# Revit family: 5.Электрический нагреватель для прямоугольных каналов ELN
name_source: partatom
category: Оборудование
revit_build: Autodesk Revit 2016 (Build: 20151209_0715(x64)
units: mm (PartAtom-declared; Revit-internal decimal feet)

## family parameters
Всегда вертикально = Да
На основе рабочей плоскости = Нет
Общий = Нет
При загрузке вырезать с полостями = Нет
Размер круглого соединителя = Использовать диаметр
Тип детали = Нормальный
Точка расчета площади = Нет

## types (29) — shared parameters
d = 15 мм
Единица измерения = шт.
Завод изготовитель = KORF
Ключевая пометка = Вентиляция
Материал = Сталь серая
Наименование и тех.хар-ка = Электрический нагреватель для прямоугольных каналов
Раздел = ОВ

## per-type parameters (varying)
| type | А | Б | Б2 | Высота | Г | Глубина среза | Д | Е | Ж | Ж2 | И | И1 | К | Масса единицы | Мощность, кВт | Напряжение U,В | Размер В | Сила тока J, А | Тип, марка, обозначение | Ширина |
| 30-15/3 | 300 мм | 150 мм | 21 мм | 150 мм | 170 мм | 15 мм | 340 мм | 190 мм | 410 мм | 35 мм | 360 мм | 356 мм | 9 мм | 7 кг | 3 Вт | 1-220 | 320 мм | 13,1 | ELN 30-15/3 | 300 мм |
| 30-15/4.5 | 300 мм | 150 мм | 21 мм | 150 мм | 170 мм | 15 мм | 340 мм | 190 мм | 410 мм | 35 мм | 360 мм | 356 мм | 9 мм | 7.4 кг | 5 Вт | 1-220 | 320 мм | 19,1 | ELN 30-15/4.5 | 300 мм |
| 40-20/6 | 400 мм | 200 мм | 27 мм | 200 мм | 220 мм | 15 мм | 440 мм | 240 мм | 510 мм | 35 мм | 390 мм | 386 мм | 9 мм | 16 кг | 6 Вт | 3-380 | 420 мм | 9,1 | ELN 40-20/6 | 400 мм |
| 40-20/12 | 400 мм | 200 мм | 27 мм | 200 мм | 220 мм | 15 мм | 440 мм | 240 мм | 510 мм | 35 мм | 510 мм | 506 мм | 9 мм | 16 кг | 12 Вт | 3-380 | 420 мм | 18,1 | ELN 40-20/12 | 400 мм |
| 50-25/7.5 | 500 мм | 250 мм | 32 мм | 250 мм | 270 мм | 15 мм | 540 мм | 290 мм | 610 мм | 35 мм | 390 мм | 386 мм | 9 мм | 11 кг | 8 Вт | 3-380 | 520 мм | 11,3 | ELN 50-25/7.5 | 500 мм |
| 50-25/15 | 500 мм | 250 мм | 32 мм | 250 мм | 270 мм | 15 мм | 540 мм | 290 мм | 610 мм | 35 мм | 510 мм | 506 мм | 9 мм | 15 кг | 15 Вт | 3-380 | 520 мм | 22,6 | ELN 50-25/15 | 500 мм |
| 50-25/22.5 | 500 мм | 250 мм | 32 мм | 250 мм | 270 мм | 15 мм | 540 мм | 290 мм | 610 мм | 35 мм | 630 мм | 626 мм | 9 мм | 19 кг | 23 Вт | 3-380 | 520 мм | 33,9 | ELN 50-25/22.5 | 500 мм |
| 50-30/7.5 | 500 мм | 300 мм | 38 мм | 300 мм | 320 мм | 15 мм | 540 мм | 340 мм | 610 мм | 35 мм | 390 мм | 386 мм | 9 мм | 11.5 кг | 8 Вт | 3-380 | 520 мм | 11,3 | ELN 50-30/7.5 | 500 мм |
| 50-30/15 | 500 мм | 300 мм | 38 мм | 300 мм | 320 мм | 15 мм | 540 мм | 340 мм | 610 мм | 35 мм | 510 мм | 506 мм | 9 мм | 15.7 кг | 15 Вт | 3-380 | 520 мм | 22,6 | ELN 50-30/15 | 500 мм |
| 50-30/22.5 | 500 мм | 300 мм | 38 мм | 300 мм | 320 мм | 15 мм | 540 мм | 340 мм | 610 мм | 35 мм | 630 мм | 626 мм | 9 мм | 19.8 кг | 23 Вт | 3-380 | 520 мм | 33,9 | ELN 50-30/22.5 | 500 мм |
| 60-30/15 | 600 мм | 300 мм | 38 мм | 300 мм | 320 мм | 15 мм | 640 мм | 340 мм | 710 мм | 35 мм | 510 мм | 506 мм | 9 мм | 16.8 кг | 15 Вт | 3-380 | 620 мм | 22,6 | ELN 60-30/15 | 600 мм |
| 60-30/22.5 | 600 мм | 300 мм | 38 мм | 300 мм | 320 мм | 15 мм | 640 мм | 340 мм | 710 мм | 35 мм | 630 мм | 626 мм | 9 мм | 22.4 кг | 23 Вт | 3-380 | 620 мм | 33,9 | ELN 60-30/22.5 | 600 мм |
| 60-30/30 | 600 мм | 300 мм | 38 мм | 300 мм | 320 мм | 15 мм | 640 мм | 340 мм | 710 мм | 35 мм | 750 мм | 746 мм | 9 мм | 26.4 кг | 30 Вт | 3-380 | 620 мм | 45,1 | ELN 60-30/30 | 600 мм |
| 60-35/15 | 600 мм | 350 мм | 43 мм | 350 мм | 370 мм | 15 мм | 640 мм | 390 мм | 710 мм | 35 мм | 510 мм | 506 мм | 9 мм | 17.5 кг | 15 Вт | 3-380 | 620 мм | 22,6 | ELN 60-35/15 | 600 мм |
| 60-35/22.5 | 600 мм | 350 мм | 43 мм | 350 мм | 370 мм | 15 мм | 640 мм | 390 мм | 710 мм | 35 мм | 630 мм | 626 мм | 9 мм | 24.6 кг | 23 Вт | 3-380 | 620 мм | 33,9 | ELN 60-35/22.5 | 600 мм |
| 60-35/30 | 600 мм | 350 мм | 43 мм | 350 мм | 370 мм | 15 мм | 640 мм | 390 мм | 710 мм | 35 мм | 750 мм | 746 мм | 9 мм | 28.4 кг | 30 Вт | 3-380 | 620 мм | 45,1 | ELN 60-35/30 | 600 мм |
| 70-40/15 | 700 мм | 400 мм | 49 мм | 400 мм | 420 мм | 15 мм | 740 мм | 440 мм | 812 мм | 36 мм | 510 мм | 506 мм | 9 мм | 26.7 кг | 15 Вт | 3-380 | 720 мм | 22,6 | ELN 70-40/15 | 700 мм |
| 70-40/30 | 700 мм | 400 мм | 49 мм | 400 мм | 420 мм | 15 мм | 740 мм | 440 мм | 812 мм | 36 мм | 510 мм | 506 мм | 9 мм | 27.1 кг | 30 Вт | 3-380 | 720 мм | 45,1 | ELN 70-40/30 | 700 мм |
| 70-40/45 | 700 мм | 400 мм | 49 мм | 400 мм | 420 мм | 15 мм | 740 мм | 440 мм | 830 мм | 45 мм | 750 мм | 746 мм | 9 мм | 41.2 кг | 45 Вт | 3-380 | 720 мм | 67,6 | ELN 70-40/45 | 700 мм |
| 70-40/60 | 700 мм | 400 мм | 49 мм | 400 мм | 420 мм | 15 мм | 740 мм | 440 мм | 830 мм | 45 мм | 750 мм | 746 мм | 9 мм | 41.2 кг | 60 Вт | 3-380 | 720 мм | 90,1 | ELN 70-40/60 | 700 мм |
| 80-50/15 | 800 мм | 500 мм | 60 мм | 500 мм | 520 мм | 15 мм | 840 мм | 540 мм | 910 мм | 35 мм | 510 мм | 506 мм | 9 мм | 31.1 кг | 15 Вт | 3-380 | 820 мм | 22,6 | ELN 80-50/15 | 800 мм |
| 80-50/30 | 800 мм | 500 мм | 60 мм | 500 мм | 520 мм | 15 мм | 840 мм | 540 мм | 910 мм | 35 мм | 510 мм | 506 мм | 9 мм | 31.4 кг | 30 Вт | 3-380 | 820 мм | 45,1 | ELN 80-50/30 | 800 мм |
| 80-50/45 | 800 мм | 500 мм | 60 мм | 500 мм | 520 мм | 15 мм | 840 мм | 540 мм | 930 мм | 45 мм | 750 мм | 746 мм | 9 мм | 45.2 кг | 45 Вт | 3-380 | 820 мм | 67,6 | ELN 80-50/45 | 800 мм |
| 80-50/60 | 800 мм | 500 мм | 60 мм | 500 мм | 520 мм | 15 мм | 840 мм | 540 мм | 930 мм | 45 мм | 750 мм | 746 мм | 9 мм | 45.2 кг | 60 Вт | 3-380 | 820 мм | 90,1 | ELN 80-50/60 | 800 мм |
| 90-50/30 | 900 мм | 500 мм | 62 мм | 500 мм | 530 мм | 16 мм | 960 мм | 560 мм | 960 мм | 0 мм | 513 мм | 509 мм | 11 мм | 31.5 кг | 30 Вт | 3-380 | 930 мм | 45,1 | ELN 90-50/30 | 900 мм |
| 90-50/45 | 900 мм | 500 мм | 62 мм | 500 мм | 530 мм | 16 мм | 960 мм | 560 мм | 960 мм | 0 мм | 753 мм | 749 мм | 11 мм | 49.8 кг | 45 Вт | 3-380 | 930 мм | 67,6 | ELN 90-50/45 | 900 мм |
| 90-50/60 | 900 мм | 500 мм | 62 мм | 500 мм | 530 мм | 16 мм | 960 мм | 560 мм | 960 мм | 0 мм | 753 мм | 749 мм | 11 мм | 49.8 кг | 60 Вт | 3-380 | 930 мм | 90,1 | ELN 90-50/60 | 900 мм |
| 100-50/45 | 1000 мм | 500 мм | 62 мм | 500 мм | 530 мм | 16 мм | 1060 мм | 560 мм | 1060 мм | 0 мм | 753 мм | 749 мм | 11 мм | 51 кг | 45 Вт | 3-380 | 1030 мм | 67,6 | ELN 100-50/45 | 1000 мм |
| 100-50/60 | 1000 мм | 500 мм | 62 мм | 500 мм | 530 мм | 16 мм | 1060 мм | 560 мм | 1060 мм | 0 мм | 753 мм | 749 мм | 11 мм | 51 кг | 60 Вт | 3-380 | 1030 мм | 90,1 | ELN 100-50/60 | 1000 мм |
